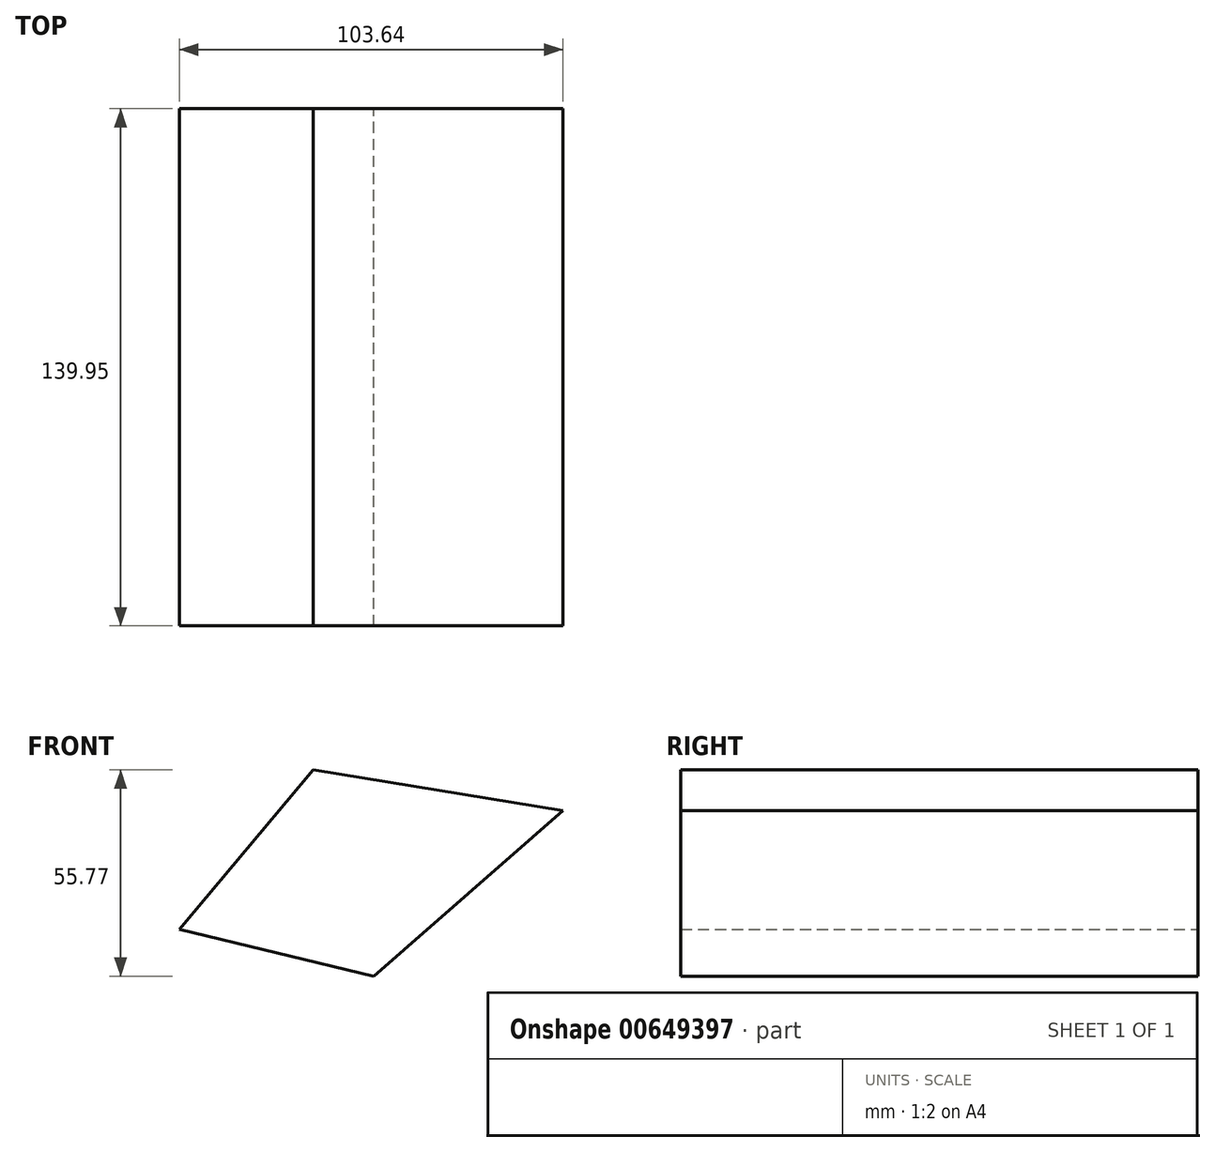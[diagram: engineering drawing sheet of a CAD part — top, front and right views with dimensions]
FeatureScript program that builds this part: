
annotation { "Feature Type Name" : "Feature", "Feature Type Description" : "" }
export const myFeature = defineFeature(function(context is Context, id is Id, definition is map)
    precondition{}
    {
        {
            var Q0;
            Q0=qCreatedBy(makeId("Front.planeOp"),FACE);
            var sketch = newSketch(context, id + "F0", { "sketchPlane" : qUnion([Q0])});
            skLineSegment(sketch, "E0", {"start": v(-105.62, 0) * mm, "end": v(-38.15, -11.01) * mm});
            skLineSegment(sketch, "E1", {"start": v(-38.15, -11.01) * mm, "end": v(-89.3, -55.77) * mm});
            skLineSegment(sketch, "E2", {"start": v(-89.3, -55.77) * mm, "end": v(-141.79, -43.14) * mm});
            skLineSegment(sketch, "E3", {"start": v(-141.79, -43.14) * mm, "end": v(-105.62, 0) * mm});
            skSolve(sketch);
        }
        {
            var Q0;
            Q0 = qSketchRegion(id + "F0", true);
            extrude(context, id + "F1", {"entities" : qUnion([Q0]), "depth" : 139.95 * mm, "offsetDistance" : 25.4 * mm});
        }
    });
